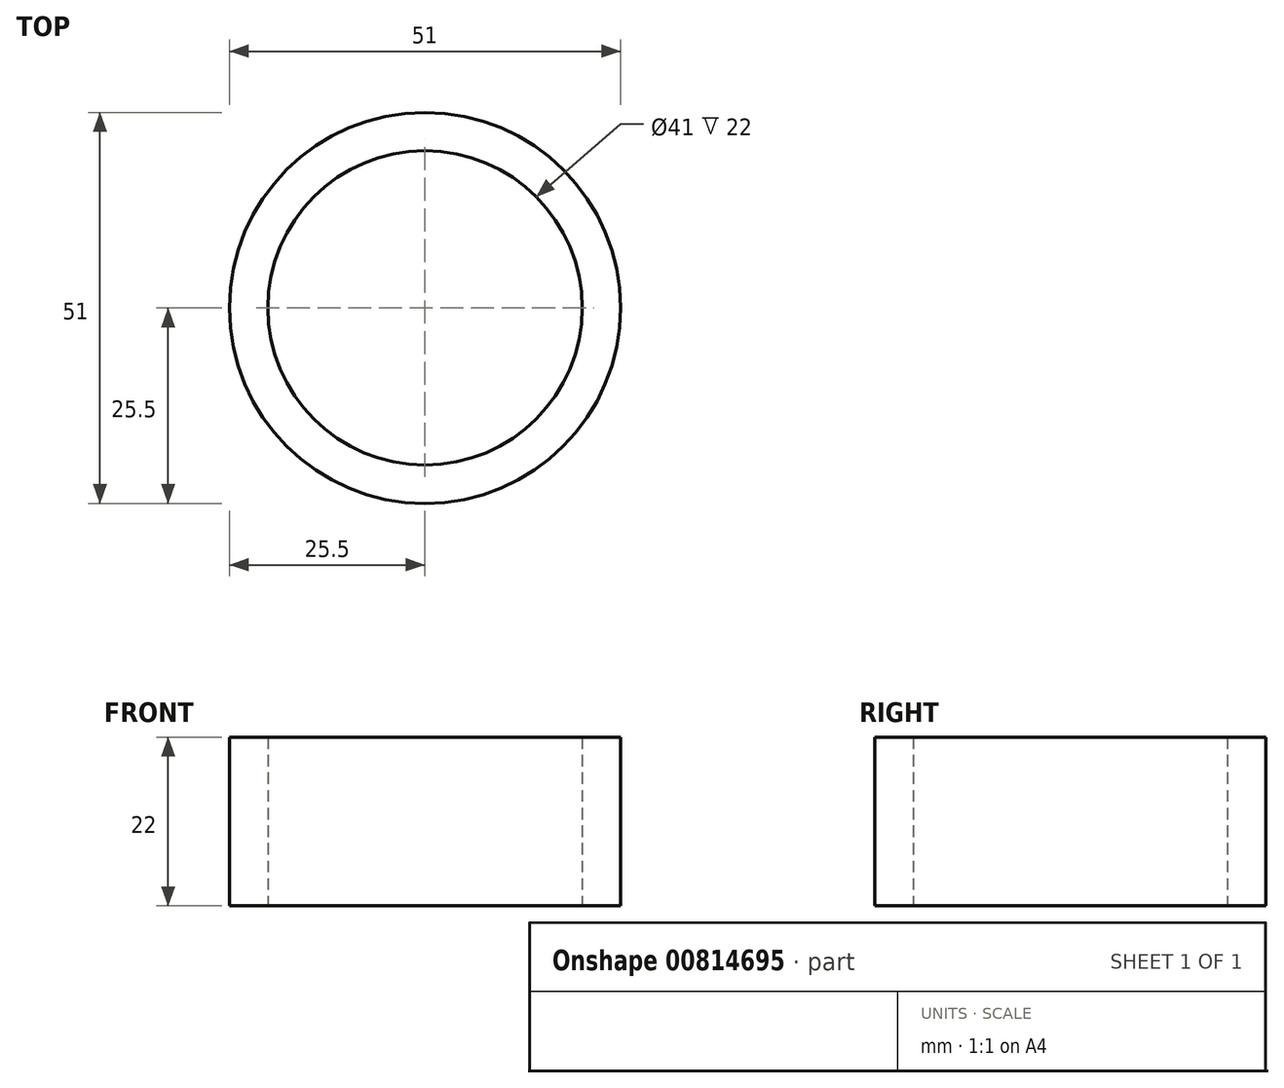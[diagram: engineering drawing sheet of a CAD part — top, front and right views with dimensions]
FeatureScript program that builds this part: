
annotation { "Feature Type Name" : "Feature", "Feature Type Description" : "" }
export const myFeature = defineFeature(function(context is Context, id is Id, definition is map)
    precondition{}
    {
        {
            var Q0;
            Q0=qCreatedBy(makeId("Top.planeOp"),FACE);
            var sketch = newSketch(context, id + "F0", { "sketchPlane" : qUnion([Q0])});
            skCircle(sketch, "E0", {"center": v(0, 0) * mm, "radius": 20.5 * mm});
            skCircle(sketch, "E1.0", {"center": v(0, 0) * mm, "radius": 25.5 * mm});
            skSolve(sketch);
        }
        {
            var Q0;
            Q0=makeQuery(id+"F0.imprint","IMPRINT",FACE,{"disambiguationData":[TD([[makeQuery(id+"F0.imprint","IMPRINT",EDGE,{"derivedFrom":sQuery(id+"F0.wireOp",EDGE,"E0")}),-1.0]])]});
            extrude(context, id + "F1", {"entities" : qUnion([Q0]), "depth" : 22 * mm, "offsetDistance" : 25 * mm});
        }
        {
            var Q0;
            Q0=qCreatedBy(makeId("Top.planeOp"),FACE);
            cPlane(context, id + "F2", {"entities" : qUnion([Q0]), "cplaneType" : CPlaneType.OFFSET, "offset" : 82 * mm, "width" : 150 * mm, "height" : 150 * mm});
        }
    });
